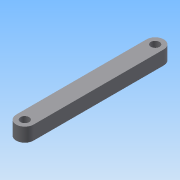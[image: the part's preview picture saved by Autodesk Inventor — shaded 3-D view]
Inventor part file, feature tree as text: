
AUTODESK INVENTOR PART (.ipt)
format: ipt  version: 2015 (Build 190159000, 159)  size: 76,800 bytes
history: native  units: mm
features: other x1, extrude x1, sketch x1
ambient origin geometry x8: Origin, YZ Plane, XZ Plane, XY Plane, X Axis, Y Axis, Z Axis, Center Point
bodies: Body1 (feature_tree)
feature tree (3):
  other  "實體1"
  extrude  "擠出1"  Depth=18.78mm
  sketch  "草圖1"
